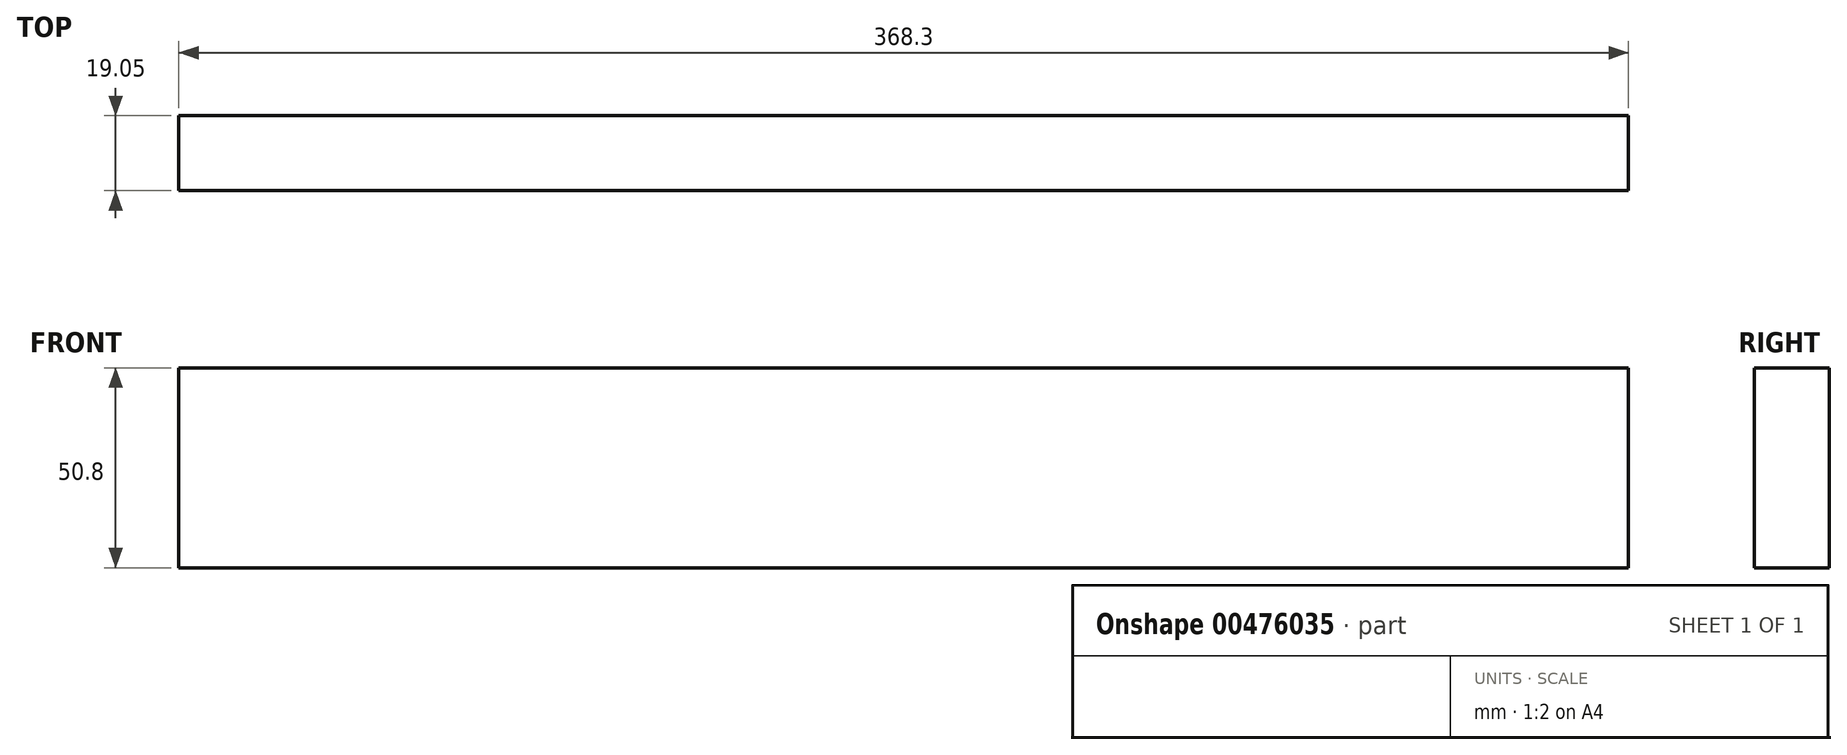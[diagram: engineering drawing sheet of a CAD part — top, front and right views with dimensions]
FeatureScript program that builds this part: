
annotation { "Feature Type Name" : "Feature", "Feature Type Description" : "" }
export const myFeature = defineFeature(function(context is Context, id is Id, definition is map)
    precondition{}
    {
        {
            var Q0;
            Q0=qCreatedBy(makeId("Front.planeOp"),FACE);
            var sketch = newSketch(context, id + "F0", { "sketchPlane" : qUnion([Q0])});
            skLineSegment(sketch, "E0.bottom", {"start": v(0, 0) * mm, "end": v(368.3, 0) * mm});
            skLineSegment(sketch, "E0.top", {"start": v(0, 50.8) * mm, "end": v(368.3, 50.8) * mm});
            skLineSegment(sketch, "E0.left", {"start": v(0, 0) * mm, "end": v(0, 50.8) * mm});
            skLineSegment(sketch, "E0.right", {"start": v(368.3, 0) * mm, "end": v(368.3, 50.8) * mm});
            skSolve(sketch);
        }
        {
            var Q0;
            Q0 = qSketchRegion(id + "F0", true);
            extrude(context, id + "F1", {"entities" : qUnion([Q0]), "depth" : 19.05 * mm});
        }
    });
